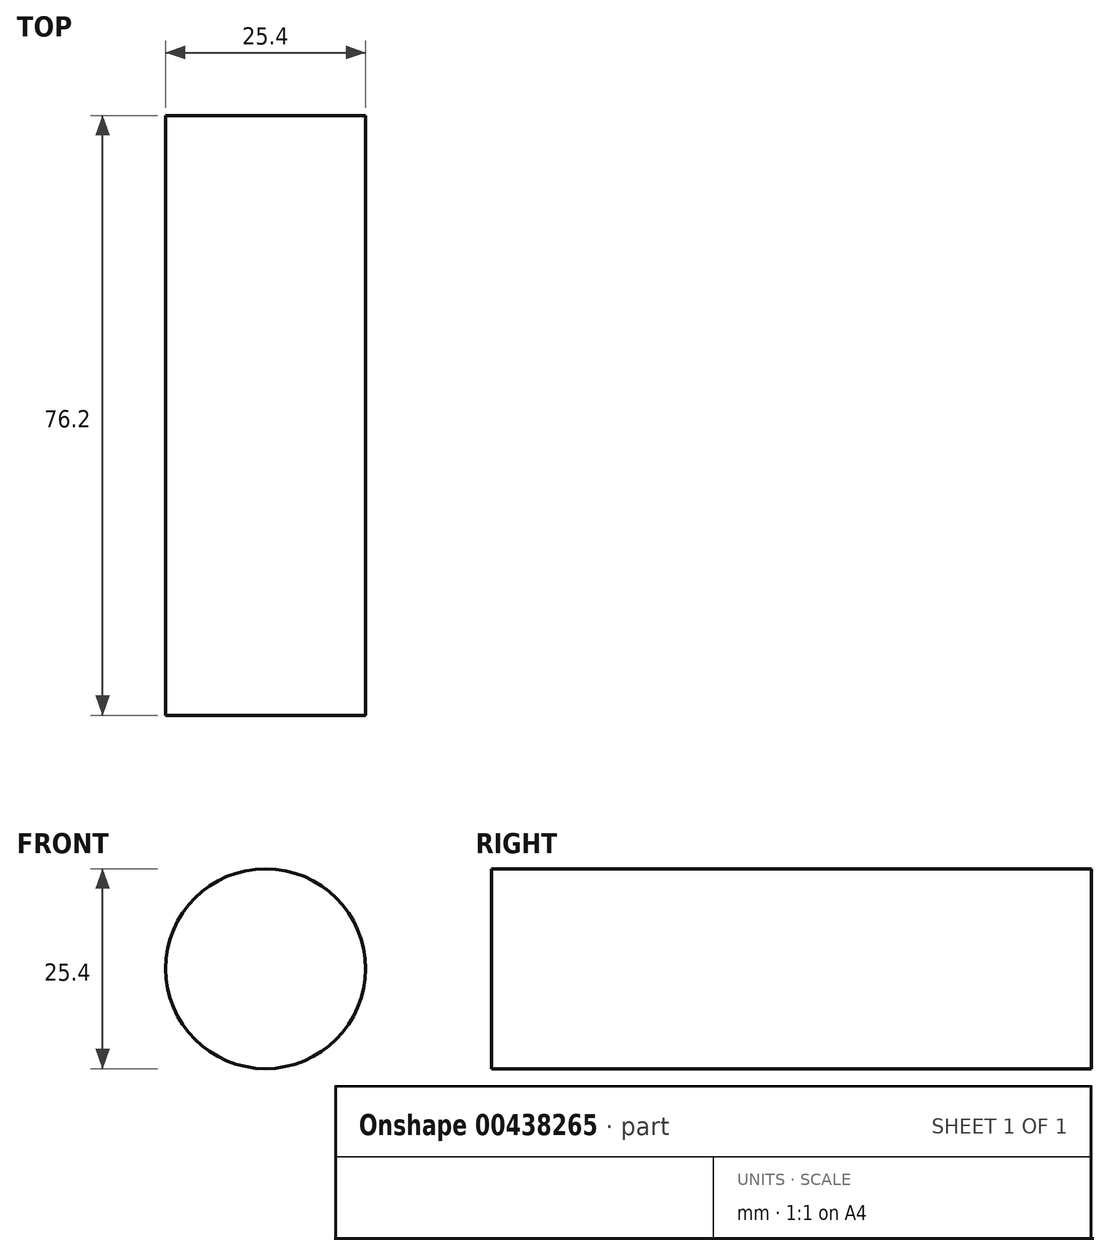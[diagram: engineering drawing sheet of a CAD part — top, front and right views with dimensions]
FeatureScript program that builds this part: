
annotation { "Feature Type Name" : "Feature", "Feature Type Description" : "" }
export const myFeature = defineFeature(function(context is Context, id is Id, definition is map)
    precondition{}
    {
        {
            var Q0;
            Q0=qCreatedBy(makeId("Front.planeOp"),FACE);
            var sketch = newSketch(context, id + "F0", { "sketchPlane" : qUnion([Q0])});
            skCircle(sketch, "E0", {"center": v(-43.48, 48.44) * mm, "radius": 12.7 * mm});
            skSolve(sketch);
        }
        {
            var Q0;
            Q0=makeQuery(id+"F0.imprint","IMPRINT",FACE,{"disambiguationData":[TD([[makeQuery(id+"F0.imprint","IMPRINT",EDGE,{"derivedFrom":sQuery(id+"F0.wireOp",EDGE,"E0")}),1.0]])]});
            extrude(context, id + "F1", {"entities" : qUnion([Q0]), "depth" : 76.2 * mm});
        }
    });
